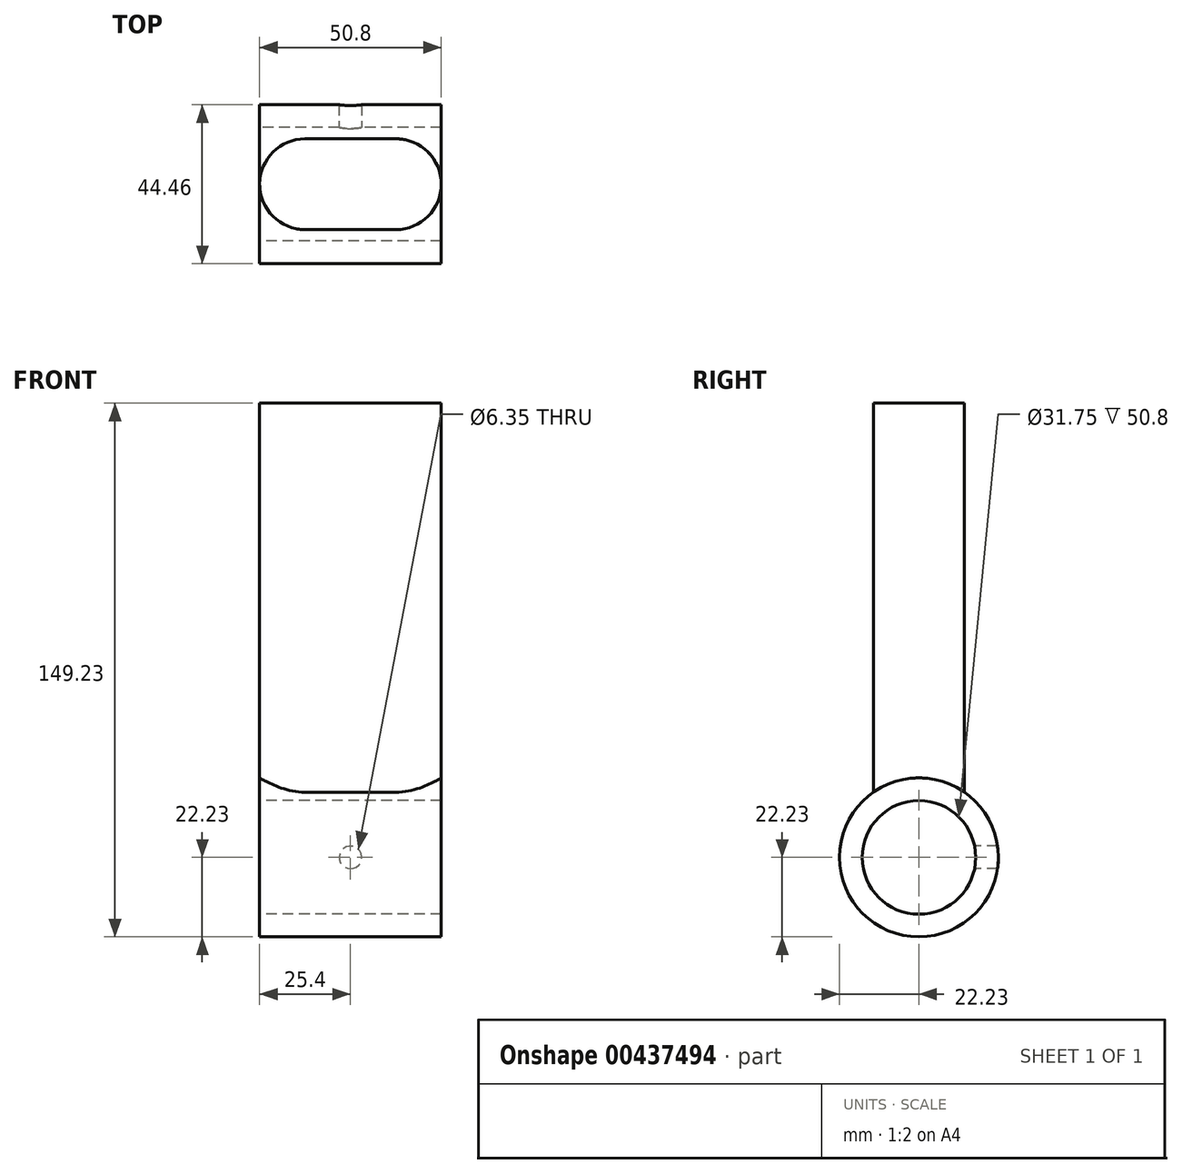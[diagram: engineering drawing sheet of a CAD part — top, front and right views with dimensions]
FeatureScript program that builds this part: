
annotation { "Feature Type Name" : "Feature", "Feature Type Description" : "" }
export const myFeature = defineFeature(function(context is Context, id is Id, definition is map)
    precondition{}
    {
        {
            var Q0;
            Q0=qCreatedBy(makeId("Right.planeOp"),FACE);
            var sketch = newSketch(context, id + "F0", { "sketchPlane" : qUnion([Q0])});
            skCircle(sketch, "E0", {"center": v(0, 0) * mm, "radius": 22.23 * mm});
            skCircle(sketch, "E1", {"center": v(0, 0) * mm, "radius": 15.88 * mm});
            skSolve(sketch);
        }
        {
            var Q0;
            Q0=makeQuery(id+"F0.imprint","IMPRINT",FACE,{"disambiguationData":[TD([[makeQuery(id+"F0.imprint","IMPRINT",EDGE,{"derivedFrom":sQuery(id+"F0.wireOp",EDGE,"E0")}),1.0]])]});
            extrude(context, id + "F1", {"entities" : qUnion([Q0]), "depth" : 50.8 * mm});
        }
        {
            var Q0;
            Q0=qCreatedBy(makeId("Front.planeOp"),FACE);
            var sketch = newSketch(context, id + "F2", { "sketchPlane" : qUnion([Q0])});
            skCircle(sketch, "E2", {"center": v(25.4, 0) * mm, "radius": 3.18 * mm});
            skSolve(sketch);
        }
        {
            var Q0;
            Q0 = qSketchRegion(id + "F2", true);
            extrude(context, id + "F3", {"entities" : qUnion([Q0]), "operationType" : NewBodyOperationType.REMOVE, "oppositeDirection" : true, "depth" : 37.6 * mm});
        }
        {
            var Q0;
            Q0=qCreatedBy(makeId("Top.planeOp"),FACE);
            var sketch = newSketch(context, id + "F4", { "sketchPlane" : qUnion([Q0])});
            skLineSegment(sketch, "E3", {"start": v(0, 0) * mm, "end": v(12.7, 0) * mm});
            skLineSegment(sketch, "E4", {"start": v(12.7, 0) * mm, "end": v(38.1, 0) * mm});
            skCircle(sketch, "E5", {"center": v(12.7, 0) * mm, "radius": 12.7 * mm});
            skCircle(sketch, "E6", {"center": v(38.1, 0) * mm, "radius": 12.7 * mm});
            skLineSegment(sketch, "E7", {"start": v(12.7, -12.7) * mm, "end": v(38.1, -12.7) * mm});
            skLineSegment(sketch, "E8", {"start": v(38.1, -12.7) * mm, "end": v(38.1, 12.7) * mm});
            skLineSegment(sketch, "E9", {"start": v(38.1, 12.7) * mm, "end": v(12.7, 12.7) * mm});
            skLineSegment(sketch, "E10", {"start": v(12.7, 12.7) * mm, "end": v(12.7, -12.7) * mm});
            skSolve(sketch);
        }
        {
            var Q0;
            Q0 = qSketchRegion(id + "F4", true);
            extrude(context, id + "F5", {"entities" : qUnion([Q0]), "operationType" : NewBodyOperationType.ADD, "depth" : 127 * mm});
        }
        {
            var Q0;
            Q0=makeQuery(id+"F1.opExtrude","CAP_FACE",FACE,{"disambiguationData":[OSD([sQuery(id+"F0.wireOp",EDGE,"E0"),sQuery(id+"F0.wireOp",EDGE,"E1")])],"isStart":false});
            var sketch = newSketch(context, id + "F6", { "sketchPlane" : qUnion([Q0])});
            skCircle(sketch, "E11", {"center": v(0, 0) * mm, "radius": 15.88 * mm});
            skSolve(sketch);
        }
        {
            var Q0;
            Q0 = qSketchRegion(id + "F6", true);
            extrude(context, id + "F7", {"entities" : qUnion([Q0]), "operationType" : NewBodyOperationType.REMOVE, "oppositeDirection" : true, "depth" : 70.1 * mm});
        }
    });
